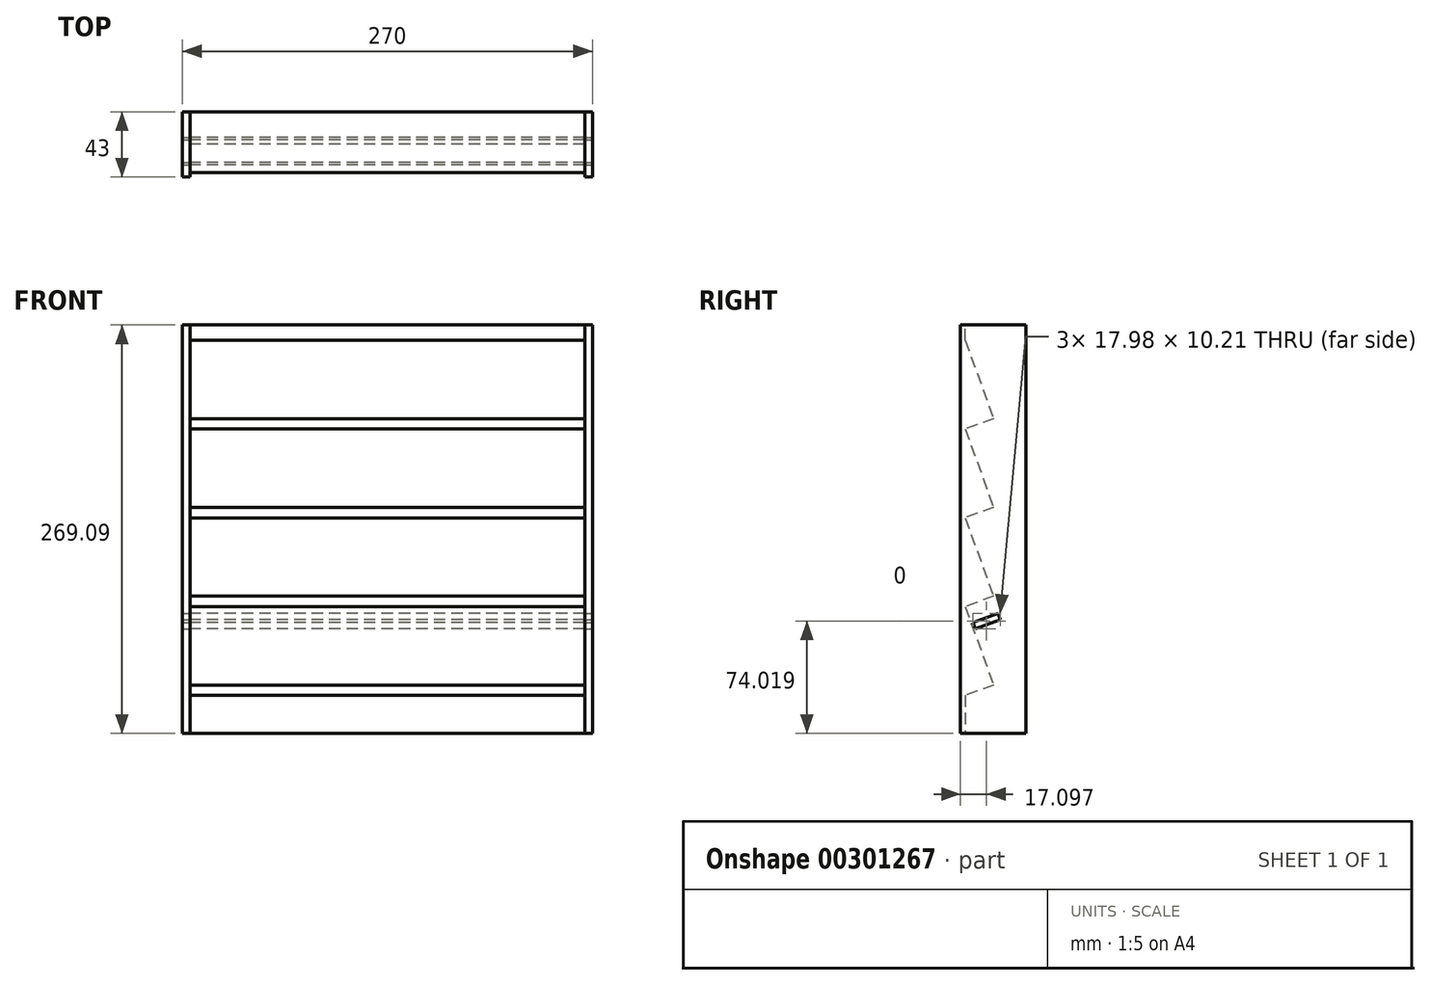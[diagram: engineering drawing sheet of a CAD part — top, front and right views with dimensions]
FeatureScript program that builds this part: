
annotation { "Feature Type Name" : "Feature", "Feature Type Description" : "" }
export const myFeature = defineFeature(function(context is Context, id is Id, definition is map)
    precondition{}
    {
        {
            assignVariable(context, id + "F0", {"name" : "thinkness", "anyValue" : 5});
        }
        {
            assignVariable(context, id + "F1", {"name" : "boxW", "anyValue" : 260});
        }
        {
            var Q0;
            Q0=qCreatedBy(makeId("Right.planeOp"),FACE);
            var sketch = newSketch(context, id + "F2", { "sketchPlane" : qUnion([Q0])});
            skLineSegment(sketch, "E0.top", {"start": v(43, 0) * mm, "end": v(0, 0) * mm});
            skLineSegment(sketch, "E0.left", {"start": v(43, 269.1) * mm, "end": v(43, 0) * mm});
            skPoint(sketch, "E1", {"position": v(3, 259.1) * mm});
            skPoint(sketch, "E2", {"position": v(3, 25) * mm});
            skLineSegment(sketch, "E3", {"start": v(3, 259.1) * mm, "end": v(21.8, 207.4) * mm});
            skLineSegment(sketch, "E4", {"start": v(21.8, 207.4) * mm, "end": v(3, 200.57) * mm});
            skLineSegment(sketch, "E5", {"start": v(3, 200.57) * mm, "end": v(21.8, 148.88) * mm});
            skLineSegment(sketch, "E6", {"start": v(21.8, 148.88) * mm, "end": v(3, 142.05) * mm});
            skLineSegment(sketch, "E7", {"start": v(3, 142.05) * mm, "end": v(21.8, 90.36) * mm});
            skLineSegment(sketch, "E8", {"start": v(21.8, 90.36) * mm, "end": v(3, 83.52) * mm});
            skLineSegment(sketch, "E9", {"start": v(3, 83.52) * mm, "end": v(21.8, 31.83) * mm});
            skLineSegment(sketch, "E10", {"start": v(21.8, 31.83) * mm, "end": v(3, 25) * mm});
            skLineSegment(sketch, "E11", {"start": v(3, 259.1) * mm, "end": v(3, 269.1) * mm});
            skLineSegment(sketch, "E12", {"start": v(0, 0) * mm, "end": v(0, 269.1) * mm});
            skLineSegment(sketch, "E13", {"start": v(3, 259.1) * mm, "end": v(3, 25) * mm, "construction": true});
            skLineSegment(sketch, "E14", {"start": v(24.55, 79.12) * mm, "end": v(8.1, 73.14) * mm});
            skLineSegment(sketch, "E15", {"start": v(8.1, 73.14) * mm, "end": v(9.64, 68.91) * mm});
            skLineSegment(sketch, "E16", {"start": v(9.64, 68.91) * mm, "end": v(26.09, 74.9) * mm});
            skLineSegment(sketch, "E17", {"start": v(26.09, 74.9) * mm, "end": v(24.55, 79.12) * mm});
            skLineSegment(sketch, "E18", {"start": v(16.33, 76.13) * mm, "end": v(12.4, 86.94) * mm, "construction": true});
            skLineSegment(sketch, "E19", {"start": v(0, 269.1) * mm, "end": v(43, 269.1) * mm});
            skLineSegment(sketch, "E20", {"start": v(3, 25) * mm, "end": v(3, 0) * mm});
            skSolve(sketch);
        }
        {
            var Q0;
            {var subQ0=sQuery(id+"F2.wireOp",EDGE,"E0.left");Q0=makeQuery(id+"F2.imprint","IMPRINT",FACE,{"disambiguationData":[TD([[makeQuery(id+"F2.imprint","IMPRINT",EDGE,{"derivedFrom":subQ0}),-1.0]])]});}
            extrude(context, id + "F3", {"entities" : qUnion([Q0]), "depth" : (getVariable(context, 'boxW')) * mm});
        }
        {
            var Q0;
            Q0=makeQuery(id+"F2.imprint","IMPRINT",FACE,{"disambiguationData":[TD([[makeQuery(id+"F2.imprint","IMPRINT",EDGE,{"derivedFrom":sQuery(id+"F2.wireOp",EDGE,"E3")}),-1.0]])]});
            var Q1;
            {var subQ0=sQuery(id+"F2.wireOp",EDGE,"E0.left");Q1=makeQuery(id+"F2.imprint","IMPRINT",FACE,{"disambiguationData":[TD([[makeQuery(id+"F2.imprint","IMPRINT",EDGE,{"derivedFrom":subQ0}),-1.0]])]});}
            extrude(context, id + "F4", {"entities" : qUnion([Q0, Q1]), "oppositeDirection" : true, "depth" : (getVariable(context, 'thinkness')) * mm});
        }
        {
            var Q0;
            Q0=makeQuery(id+"F4.opExtrude","SWEPT_BODY",BODY,{"disambiguationData":[OSD([sQuery(id+"F2.wireOp",EDGE,"E0.bottom"),sQuery(id+"F2.wireOp",EDGE,"E0.top"),sQuery(id+"F2.wireOp",EDGE,"E0.left"),sQuery(id+"F2.wireOp",EDGE,"E0.right"),sQuery(id+"F2.wireOp",EDGE,"E12")])]});
            var Q1;
            Q1=makeQuery(id+"F3.opExtrude","SWEPT_EDGE",EDGE,{"disambiguationData":[OSD([sQuery(id+"F2.wireOp",EDGE,"E0.top"),sQuery(id+"F2.wireOp",EDGE,"E0.left")])]});
            transform(context, id + "F5", {"entities" : qUnion([Q0]), "transformType" : TransformType.TRANSLATION_DISTANCE, "transformDirection" : qUnion([Q1]), "distance" : (getVariable(context, 'boxW') + getVariable(context, 'thinkness')) * mm, "oppositeDirection" : true, "makeCopy" : true});
        }
    });
